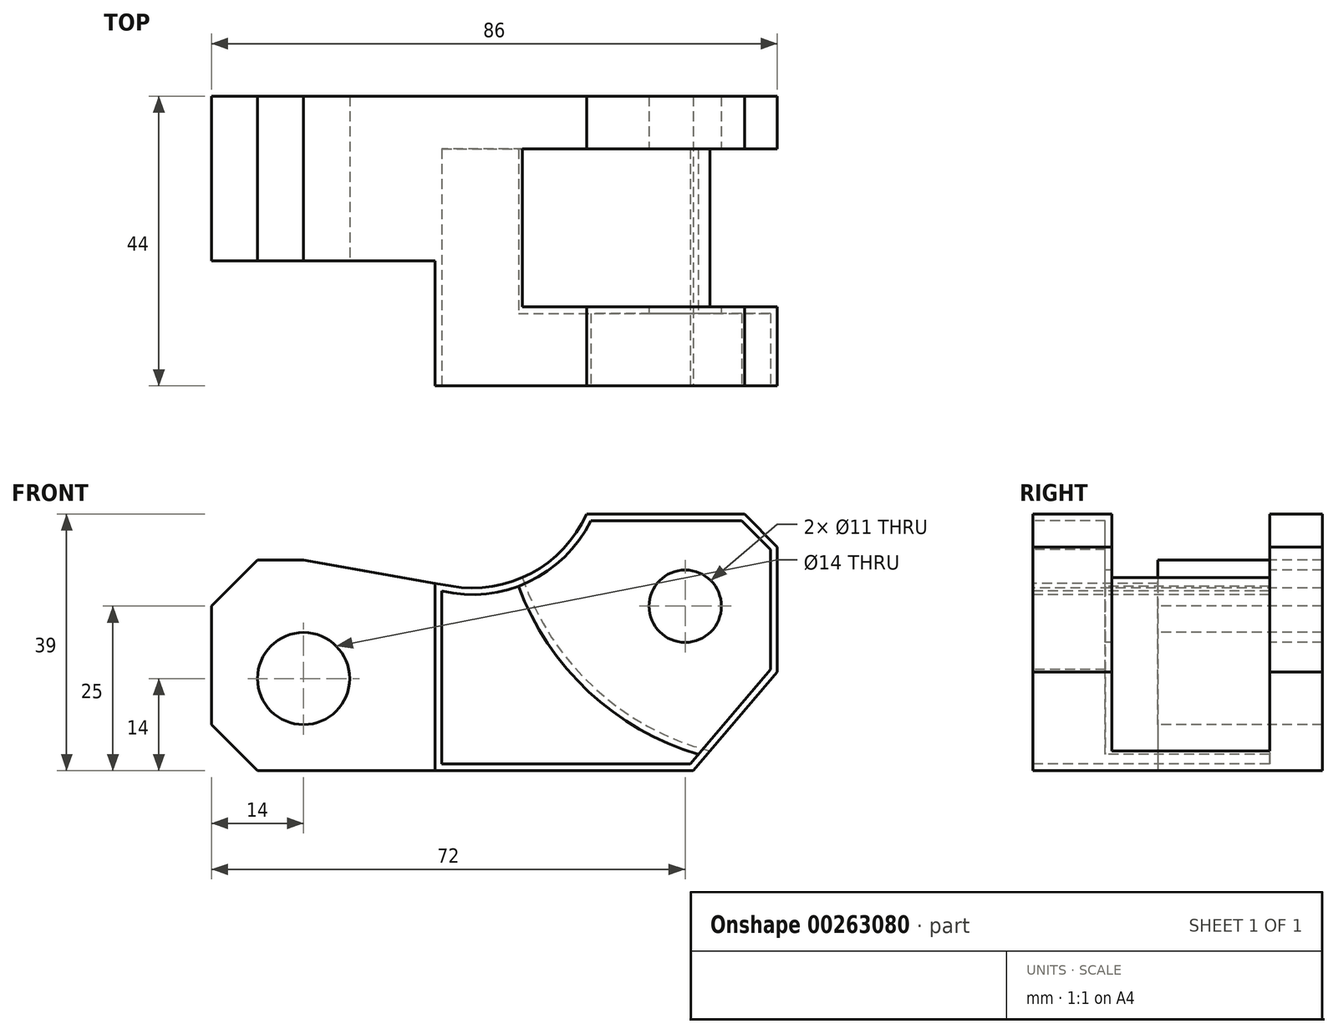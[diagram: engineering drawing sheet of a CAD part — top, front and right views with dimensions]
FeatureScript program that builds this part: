
annotation { "Feature Type Name" : "Feature", "Feature Type Description" : "" }
export const myFeature = defineFeature(function(context is Context, id is Id, definition is map)
    precondition{}
    {
        {
            var Q0;
            Q0=qCreatedBy(makeId("Front.planeOp"),FACE);
            var sketch = newSketch(context, id + "F0", { "sketchPlane" : qUnion([Q0])});
            skCircle(sketch, "E0", {"center": v(0, 0) * mm, "radius": 7 * mm});
            skLineSegment(sketch, "E1", {"start": v(-14, -7) * mm, "end": v(-14, 11) * mm});
            skLineSegment(sketch, "E2", {"start": v(-14, 11) * mm, "end": v(-7, 18) * mm});
            skLineSegment(sketch, "E3", {"start": v(-7, 18) * mm, "end": v(0, 18) * mm});
            skLineSegment(sketch, "E4", {"start": v(0, 18) * mm, "end": v(22.36, 14.06) * mm});
            skArc(sketch, "E5", {"start": v(22.36, 14.06) * mm, "mid": v(34.56, 15.98) * mm, "end": v(43, 25) * mm});
            skLineSegment(sketch, "E6", {"start": v(-14, -7) * mm, "end": v(-7, -14) * mm});
            skLineSegment(sketch, "E7", {"start": v(-7, -14) * mm, "end": v(25.58, -14) * mm});
            skArc(sketch, "E8", {"start": v(25.58, -14) * mm, "mid": v(28.84, -15.21) * mm, "end": v(30.52, -18.26) * mm});
            skArc(sketch, "E9", {"start": v(30.52, -18.26) * mm, "mid": v(32.86, -26.12) * mm, "end": v(37.3, -33) * mm});
            skLineSegment(sketch, "E10", {"start": v(37.3, -33) * mm, "end": v(43, -33) * mm});
            skLineSegment(sketch, "E11", {"start": v(43, -33) * mm, "end": v(72, 1) * mm});
            skLineSegment(sketch, "E12", {"start": v(72, 1) * mm, "end": v(72, 20) * mm});
            skLineSegment(sketch, "E13", {"start": v(72, 20) * mm, "end": v(67, 25) * mm});
            skLineSegment(sketch, "E14", {"start": v(67, 25) * mm, "end": v(43, 25) * mm});
            skLineSegment(sketch, "E15", {"start": v(20, 14.47) * mm, "end": v(20, -14) * mm});
            skLineSegment(sketch, "E16", {"start": v(25.58, -14) * mm, "end": v(59.2, -14) * mm});
            skCircle(sketch, "E17", {"center": v(58, 11) * mm, "radius": 5.5 * mm});
            skSolve(sketch);
        }
        {
            var Q0;
            {var subQ5=sQuery(id+"F0.wireOp",EDGE,"E5");Q0=makeQuery(id+"F0.imprint","IMPRINT",FACE,{"disambiguationData":[TD([[makeQuery(id+"F0.imprint","IMPRINT",EDGE,{"derivedFrom":subQ5}),-1.0]])]});}
            var Q1;
            Q1=makeQuery(id+"F0.imprint","IMPRINT",FACE,{"disambiguationData":[TD([[makeQuery(id+"F0.imprint","IMPRINT",EDGE,{"derivedFrom":sQuery(id+"F0.wireOp",EDGE,"E0")}),-1.0]])]});
            var Q2;
            Q2=makeQuery(id+"F0.imprint","IMPRINT",FACE,{"disambiguationData":[TD([[makeQuery(id+"F0.imprint","IMPRINT",EDGE,{"derivedFrom":sQuery(id+"F0.wireOp",EDGE,"E8")}),1.0]])]});
            extrude(context, id + "F1", {"entities" : qUnion([Q0, Q1, Q2]), "oppositeDirection" : true, "depth" : 44 * mm});
        }
        {
            var Q0;
            Q0=makeQuery(id+"F0.imprint","IMPRINT",FACE,{"disambiguationData":[TD([[makeQuery(id+"F0.imprint","IMPRINT",EDGE,{"derivedFrom":sQuery(id+"F0.wireOp",EDGE,"E0")}),-1.0]])]});
            var Q1;
            Q1=makeQuery(id+"F0.imprint","IMPRINT",FACE,{"disambiguationData":[TD([[makeQuery(id+"F0.imprint","IMPRINT",EDGE,{"derivedFrom":sQuery(id+"F0.wireOp",EDGE,"E8")}),1.0]])]});
            extrude(context, id + "F2", {"entities" : qUnion([Q0, Q1]), "operationType" : NewBodyOperationType.REMOVE, "oppositeDirection" : true, "depth" : 19 * mm});
        }
        {
            var Q0;
            Q0=qCreatedBy(makeId("Front.planeOp"),FACE);
            cPlane(context, id + "F3", {"entities" : qUnion([Q0]), "cplaneType" : CPlaneType.OFFSET, "offset" : 12 * mm, "oppositeDirection" : true, "width" : 150 * mm, "height" : 150 * mm});
        }
        {
            var Q0;
            Q0=qCreatedBy(id+"F3.planeOp",FACE);
            var sketch = newSketch(context, id + "F4", { "sketchPlane" : qUnion([Q0])});
            skCircle(sketch, "E18", {"center": v(72, 28.7) * mm, "radius": 41 * mm});
            skPoint(sketch, "E19", {"position": v(61.76, -11) * mm});
            skSolve(sketch);
        }
        {
            var Q0;
            Q0=qSketchRegion(id+"F4",true);
            extrude(context, id + "F5", {"entities" : qUnion([Q0]), "operationType" : NewBodyOperationType.REMOVE, "oppositeDirection" : true, "depth" : 24 * mm});
        }
        {
            var Q0;
            Q0=makeQuery(id+"F1.opExtrude","CAP_FACE",FACE,{"disambiguationData":[OSD([sQuery(id+"F0.wireOp",EDGE,"E0"),sQuery(id+"F0.wireOp",EDGE,"E1"),sQuery(id+"F0.wireOp",EDGE,"E2"),sQuery(id+"F0.wireOp",EDGE,"E3"),sQuery(id+"F0.wireOp",EDGE,"E4"),sQuery(id+"F0.wireOp",EDGE,"E5"),sQuery(id+"F0.wireOp",EDGE,"E6"),sQuery(id+"F0.wireOp",EDGE,"E7"),sQuery(id+"F0.wireOp",EDGE,"E8"),sQuery(id+"F0.wireOp",EDGE,"E9"),sQuery(id+"F0.wireOp",EDGE,"E10"),sQuery(id+"F0.wireOp",EDGE,"E11"),sQuery(id+"F0.wireOp",EDGE,"E12"),sQuery(id+"F0.wireOp",EDGE,"E13"),sQuery(id+"F0.wireOp",EDGE,"E14"),sQuery(id+"F0.wireOp",EDGE,"E17")])],"isStart":true});
            var sketch = newSketch(context, id + "F6", { "sketchPlane" : qUnion([Q0])});
            skLineSegment(sketch, "E20.0", {"start": v(21, 13.32) * mm, "end": v(21, -13) * mm});
            skArc(sketch, "E20.1", {"start": v(43.64, 24) * mm, "mid": v(34.2, 14.68) * mm, "end": v(21, 13.32) * mm});
            skLineSegment(sketch, "E20.2", {"start": v(58.74, -13) * mm, "end": v(71, 1.37) * mm});
            skLineSegment(sketch, "E20.3", {"start": v(71, 1.37) * mm, "end": v(71, 19.59) * mm});
            skLineSegment(sketch, "E20.4", {"start": v(71, 19.59) * mm, "end": v(66.59, 24) * mm});
            skLineSegment(sketch, "E20.5", {"start": v(21, -13) * mm, "end": v(58.74, -13) * mm});
            skLineSegment(sketch, "E20.6", {"start": v(66.59, 24) * mm, "end": v(43.64, 24) * mm});
            skSolve(sketch);
        }
        {
            var Q0;
            Q0=makeQuery(id+"F6.imprint","IMPRINT",FACE,{"disambiguationData":[TD([[makeQuery(id+"F6.imprint","IMPRINT",EDGE,{"derivedFrom":sQuery(id+"F6.wireOp",EDGE,"E20.0")}),1.0]])]});
            extrude(context, id + "F7", {"entities" : qUnion([Q0]), "operationType" : NewBodyOperationType.REMOVE, "oppositeDirection" : true, "depth" : 11 * mm});
        }
        {
            var Q0;
            Q0=makeQuery(id+"F7.boolean.opBoolean","COPY",FACE,{"derivedFrom":makeQuery(id+"F7.opExtrude","CAP_FACE",FACE,{"disambiguationData":[OSD([sQuery(id+"F0.wireOp",EDGE,"E17"),sQuery(id+"F6.wireOp",EDGE,"E20.0"),sQuery(id+"F6.wireOp",EDGE,"E20.1"),sQuery(id+"F6.wireOp",EDGE,"E20.2"),sQuery(id+"F6.wireOp",EDGE,"E20.3"),sQuery(id+"F6.wireOp",EDGE,"E20.4"),sQuery(id+"F6.wireOp",EDGE,"E20.5"),sQuery(id+"F6.wireOp",EDGE,"E20.6")])],"isStart":false})});
            var sketch = newSketch(context, id + "F8", { "sketchPlane" : qUnion([Q0])});
            skLineSegment(sketch, "E21", {"start": v(71, 1.37) * mm, "end": v(71, 19.59) * mm});
            skLineSegment(sketch, "E22", {"start": v(58.74, -13) * mm, "end": v(71, 1.37) * mm});
            skLineSegment(sketch, "E23", {"start": v(21, -13) * mm, "end": v(58.74, -13) * mm});
            skLineSegment(sketch, "E24", {"start": v(21, 13.32) * mm, "end": v(21, -13) * mm});
            skArc(sketch, "E25", {"start": v(43.64, 24) * mm, "mid": v(34.2, 14.68) * mm, "end": v(21, 13.32) * mm});
            skLineSegment(sketch, "E26", {"start": v(66.59, 24) * mm, "end": v(43.64, 24) * mm});
            skLineSegment(sketch, "E27", {"start": v(71, 19.59) * mm, "end": v(66.59, 24) * mm});
            skCircle(sketch, "E28", {"center": v(58, 11) * mm, "radius": 5.5 * mm});
            skArc(sketch, "E29.0.1", {"start": v(61.76, -11) * mm, "mid": v(44.18, -1.42) * mm, "end": v(33.24, 15.34) * mm});
            skArc(sketch, "E29.0.3", {"start": v(33.24, 15.34) * mm, "mid": v(44.18, -1.42) * mm, "end": v(61.76, -11) * mm});
            skArc(sketch, "E30.0", {"start": v(32.3, 15.02) * mm, "mid": v(43.5, -2.15) * mm, "end": v(61.52, -11.97) * mm});
            skSolve(sketch);
        }
        {
            var Q0;
            {var subQ4=sQuery(id+"F8.wireOp",EDGE,"E23");Q0=makeQuery(id+"F8.imprint","IMPRINT",FACE,{"disambiguationData":[TD([[makeQuery(id+"F8.imprint","IMPRINT",EDGE,{"derivedFrom":subQ4}),1.0]])]});}
            var Q1;
            Q1=makeQuery(id+"F5.boolean.opBoolean","COPY",FACE,{"derivedFrom":makeQuery(id+"F5.opExtrude","CAP_FACE",FACE,{"disambiguationData":[OSD([sQuery(id+"F4.wireOp",EDGE,"E18")])],"isStart":false})});
            extrude(context, id + "F9", {"entities" : qUnion([Q0]), "operationType" : NewBodyOperationType.REMOVE, "endBound" : BoundingType.UP_TO_SURFACE, "oppositeDirection" : true, "endBoundEntityFace" : qUnion([Q1]), "depth" : 25 * mm});
        }
    });
